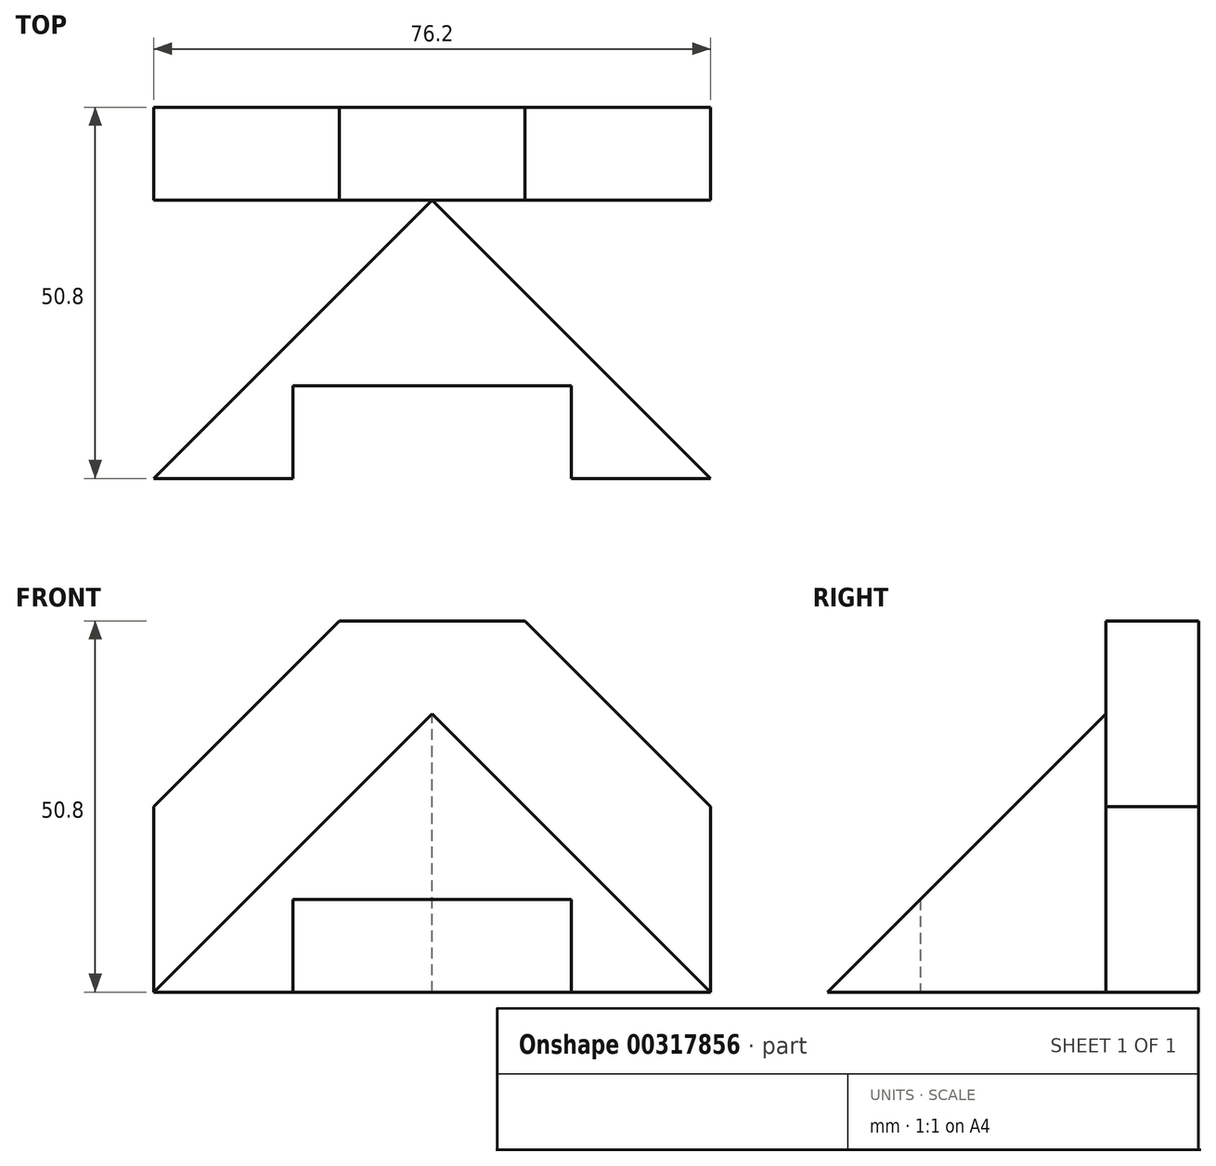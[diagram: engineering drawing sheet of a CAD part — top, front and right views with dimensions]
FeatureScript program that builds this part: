
annotation { "Feature Type Name" : "Feature", "Feature Type Description" : "" }
export const myFeature = defineFeature(function(context is Context, id is Id, definition is map)
    precondition{}
    {
        {
            var Q0;
            Q0=qCreatedBy(makeId("Right.planeOp"),FACE);
            var sketch = newSketch(context, id + "F0", { "sketchPlane" : qUnion([Q0])});
            skLineSegment(sketch, "E0", {"start": v(0, 0) * mm, "end": v(38.1, 0) * mm});
            skLineSegment(sketch, "E1", {"start": v(38.1, 0) * mm, "end": v(38.1, 38.1) * mm});
            skLineSegment(sketch, "E2", {"start": v(38.1, 38.1) * mm, "end": v(0, 0) * mm});
            skLineSegment(sketch, "E3", {"start": v(38.1, 38.1) * mm, "end": v(38.1, 50.8) * mm});
            skLineSegment(sketch, "E4", {"start": v(38.1, 50.8) * mm, "end": v(50.8, 50.8) * mm});
            skLineSegment(sketch, "E5", {"start": v(50.8, 50.8) * mm, "end": v(50.8, 0) * mm});
            skLineSegment(sketch, "E6", {"start": v(50.8, 0) * mm, "end": v(38.1, 0) * mm});
            skSolve(sketch);
        }
        {
            var Q0;
            Q0 = qSketchRegion(id + "F0", true);
            extrude(context, id + "F1", {"entities" : qUnion([Q0]), "depth" : 76.2 * mm});
        }
        {
            var Q0;
            Q0=qCreatedBy(makeId("Front.planeOp"),FACE);
            var sketch = newSketch(context, id + "F2", { "sketchPlane" : qUnion([Q0])});
            skLineSegment(sketch, "E7", {"start": v(0, 0) * mm, "end": v(0, 25.4) * mm});
            skLineSegment(sketch, "E8", {"start": v(0, 0) * mm, "end": v(76.2, 0) * mm});
            skLineSegment(sketch, "E9", {"start": v(76.2, 0) * mm, "end": v(76.2, 25.4) * mm});
            skLineSegment(sketch, "E10", {"start": v(25.4, 50.8) * mm, "end": v(50.8, 50.8) * mm});
            skLineSegment(sketch, "E11", {"start": v(0, 25.4) * mm, "end": v(25.4, 50.8) * mm});
            skLineSegment(sketch, "E12", {"start": v(50.8, 50.8) * mm, "end": v(76.2, 25.4) * mm});
            skLineSegment(sketch, "E13", {"start": v(0, 0) * mm, "end": v(38.1, 38.1) * mm});
            skLineSegment(sketch, "E14", {"start": v(38.1, 38.1) * mm, "end": v(76.2, 0) * mm});
            skLineSegment(sketch, "E15", {"start": v(0, 25.4) * mm, "end": v(0, 50.8) * mm});
            skLineSegment(sketch, "E16", {"start": v(0, 50.8) * mm, "end": v(25.4, 50.8) * mm});
            skLineSegment(sketch, "E17", {"start": v(50.8, 50.8) * mm, "end": v(76.2, 50.8) * mm});
            skLineSegment(sketch, "E18", {"start": v(76.2, 50.8) * mm, "end": v(76.2, 25.4) * mm});
            skSolve(sketch);
        }
        {
            var Q0;
            Q0=makeQuery(id+"F2.imprint","IMPRINT",FACE,{"disambiguationData":[TD([[makeQuery(id+"F2.imprint","IMPRINT",EDGE,{"derivedFrom":sQuery(id+"F2.wireOp",EDGE,"E11")}),1.0]])]});
            var Q1;
            Q1=makeQuery(id+"F2.imprint","IMPRINT",FACE,{"disambiguationData":[TD([[makeQuery(id+"F2.imprint","IMPRINT",EDGE,{"derivedFrom":sQuery(id+"F2.wireOp",EDGE,"E12")}),1.0]])]});
            extrude(context, id + "F3", {"entities" : qUnion([Q0, Q1]), "operationType" : NewBodyOperationType.REMOVE, "endBound" : BoundingType.THROUGH_ALL, "oppositeDirection" : true, "depth" : 25.4 * mm});
        }
        {
            var Q0;
            Q0=makeQuery(id+"F1.opExtrude","SWEPT_FACE",FACE,{"disambiguationData":[OSD([sQuery(id+"F0.wireOp",EDGE,"E4")])]});
            var sketch = newSketch(context, id + "F4", { "sketchPlane" : qUnion([Q0])});
            skLineSegment(sketch, "E19", {"start": v(0, 0) * mm, "end": v(38.1, 38.1) * mm});
            skLineSegment(sketch, "E20", {"start": v(38.1, 38.1) * mm, "end": v(0, 38.1) * mm});
            skLineSegment(sketch, "E21", {"start": v(0, 38.1) * mm, "end": v(0, 0) * mm});
            skLineSegment(sketch, "E22", {"start": v(38.1, 38.1) * mm, "end": v(76.2, 38.1) * mm});
            skLineSegment(sketch, "E23", {"start": v(76.2, 38.1) * mm, "end": v(76.2, 0) * mm});
            skLineSegment(sketch, "E24", {"start": v(76.2, 0) * mm, "end": v(38.1, 38.1) * mm});
            skLineSegment(sketch, "E25", {"start": v(0, 0) * mm, "end": v(76.2, 0) * mm});
            skSolve(sketch);
        }
        {
            var Q0;
            Q0=makeQuery(id+"F4.imprint","IMPRINT",FACE,{"disambiguationData":[TD([[makeQuery(id+"F4.imprint","IMPRINT",EDGE,{"derivedFrom":sQuery(id+"F4.wireOp",EDGE,"E22")}),-1.0]])]});
            var Q1;
            {var subQ0=sQuery(id+"F4.wireOp",EDGE,"E19");Q1=makeQuery(id+"F4.imprint","IMPRINT",FACE,{"disambiguationData":[TD([[makeQuery(id+"F4.imprint","IMPRINT",EDGE,{"derivedFrom":subQ0}),1.0]])]});}
            extrude(context, id + "F5", {"entities" : qUnion([Q0, Q1]), "operationType" : NewBodyOperationType.REMOVE, "endBound" : BoundingType.THROUGH_ALL, "oppositeDirection" : true, "depth" : 48.26 * mm});
        }
        {
            var Q0;
            Q0=qCreatedBy(makeId("Top.planeOp"),FACE);
            var sketch = newSketch(context, id + "F6", { "sketchPlane" : qUnion([Q0])});
            skLineSegment(sketch, "E26.bottom", {"start": v(19.05, 0) * mm, "end": v(57.15, 0) * mm});
            skLineSegment(sketch, "E26.top", {"start": v(19.05, 12.7) * mm, "end": v(57.15, 12.7) * mm});
            skLineSegment(sketch, "E26.left", {"start": v(19.05, 0) * mm, "end": v(19.05, 12.7) * mm});
            skLineSegment(sketch, "E26.right", {"start": v(57.15, 0) * mm, "end": v(57.15, 12.7) * mm});
            skSolve(sketch);
        }
        {
            var Q0;
            Q0 = qSketchRegion(id + "F6", true);
            extrude(context, id + "F7", {"entities" : qUnion([Q0]), "operationType" : NewBodyOperationType.REMOVE, "depth" : 25.4 * mm});
        }
    });
